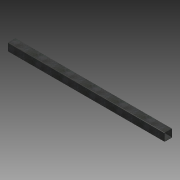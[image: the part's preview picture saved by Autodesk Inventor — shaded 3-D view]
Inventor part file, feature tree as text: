
AUTODESK INVENTOR PART (.ipt)
format: ipt  version: 2015 SP1 (Build 190203100, 203)  size: 89,088 bytes
history: native  units: in
note: dims shown in document units (in); Inventor stores cm internally (conversion verified against a paired STEP export)
features: extrude x1, fillet x1, sketch x1
ambient origin geometry x8: Origin, YZ Plane, XZ Plane, XY Plane, X Axis, Y Axis, Z Axis, Center Point
bodies: Solid1 (feature_tree)
feature tree (3):
  extrude  "Extrusion1"  Depth=2.0in
  fillet  "Fillet1"  Radius=0.083in
  sketch  "Sketch1"  dims[d0=2.0in d1=2.0in d2=0.083in d3=40.0in d4=0.0in d5=0.125in]
